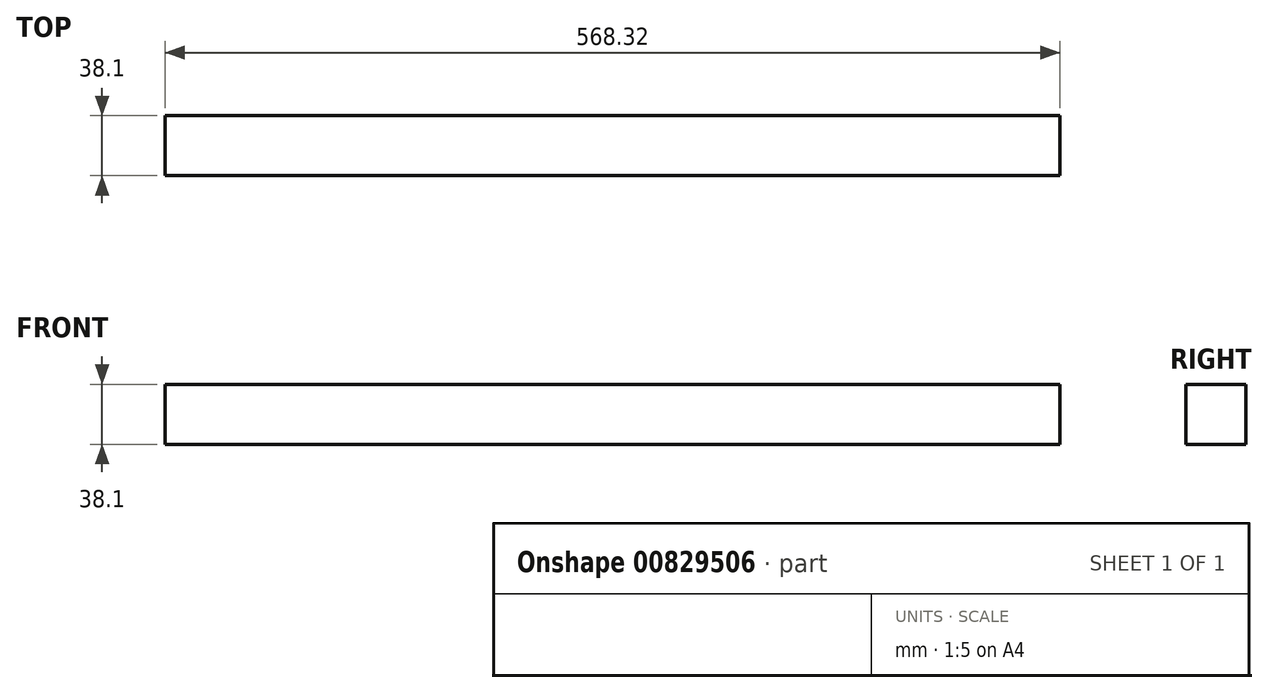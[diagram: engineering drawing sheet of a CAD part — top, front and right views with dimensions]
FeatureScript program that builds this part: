
annotation { "Feature Type Name" : "Feature", "Feature Type Description" : "" }
export const myFeature = defineFeature(function(context is Context, id is Id, definition is map)
    precondition{}
    {
        {
            var Q0;
            Q0=qCreatedBy(makeId("Right.planeOp"),FACE);
            var sketch = newSketch(context, id + "F0", { "sketchPlane" : qUnion([Q0])});
            skLineSegment(sketch, "E0.bottom", {"start": v(0, 0) * mm, "end": v(38.1, 0) * mm});
            skLineSegment(sketch, "E0.top", {"start": v(0, -38.1) * mm, "end": v(38.1, -38.1) * mm});
            skLineSegment(sketch, "E0.left", {"start": v(0, 0) * mm, "end": v(0, -38.1) * mm});
            skLineSegment(sketch, "E0.right", {"start": v(38.1, 0) * mm, "end": v(38.1, -38.1) * mm});
            skSolve(sketch);
        }
        {
            var Q0;
            Q0=makeQuery(id+"F0.imprint","IMPRINT",FACE,{"disambiguationData":[TD([[makeQuery(id+"F0.imprint","IMPRINT",EDGE,{"derivedFrom":sQuery(id+"F0.wireOp",EDGE,"E0.bottom")}),-1.0]])]});
            extrude(context, id + "F1", {"entities" : qUnion([Q0]), "depth" : 568.32 * mm, "offsetDistance" : 25.4 * mm});
        }
    });
